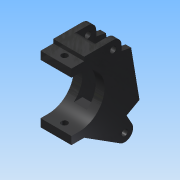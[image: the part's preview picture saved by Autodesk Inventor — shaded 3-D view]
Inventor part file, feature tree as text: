
AUTODESK INVENTOR PART (.ipt)
format: ipt  version: 2014 (Build 180170000, 170)  size: 184,832 bytes
history: native  units: in
note: dims shown in document units (in); Inventor stores cm internally (conversion verified against a paired STEP export)
features: extrude x4, sketch x4
ambient origin geometry x8: Origin, YZ Plane, XZ Plane, XY Plane, X Axis, Y Axis, Z Axis, Center Point
bodies: Solid1 (feature_tree)
feature tree (8):
  extrude  "Extrusion1"  Depth=0.125in
  extrude  "Extrusion2"  Depth=0.26in
  extrude  "Extrusion3"  Depth=1.02in
  extrude  "Extrusion4"  Depth=0.2in
  sketch  "Sketch1"  dims[d0=0.34in d1=0.125in]
  sketch  "Sketch2"  dims[d2=0.16in d3=0.26in]
  sketch  "Sketch3"  dims[d4=0.08in d5=1.02in]
  sketch  "Sketch4"  dims[d6=0.1in d7=0.2in d8=1.02in d9=0.3in d10=1.6in d11=1.39in d12=1.03in d13=0.675in d14=1.133in d15=0.4in d16=0.63in d17=0.0in d18=0.675in d19=0.125in d20=0.125in d21=0.4in d22=0.0in d23=0.27in d24=0.78in d25=0.4in d26=0.0in d27=0.125in d28=0.16in d29=0.4in d30=0.0in]
